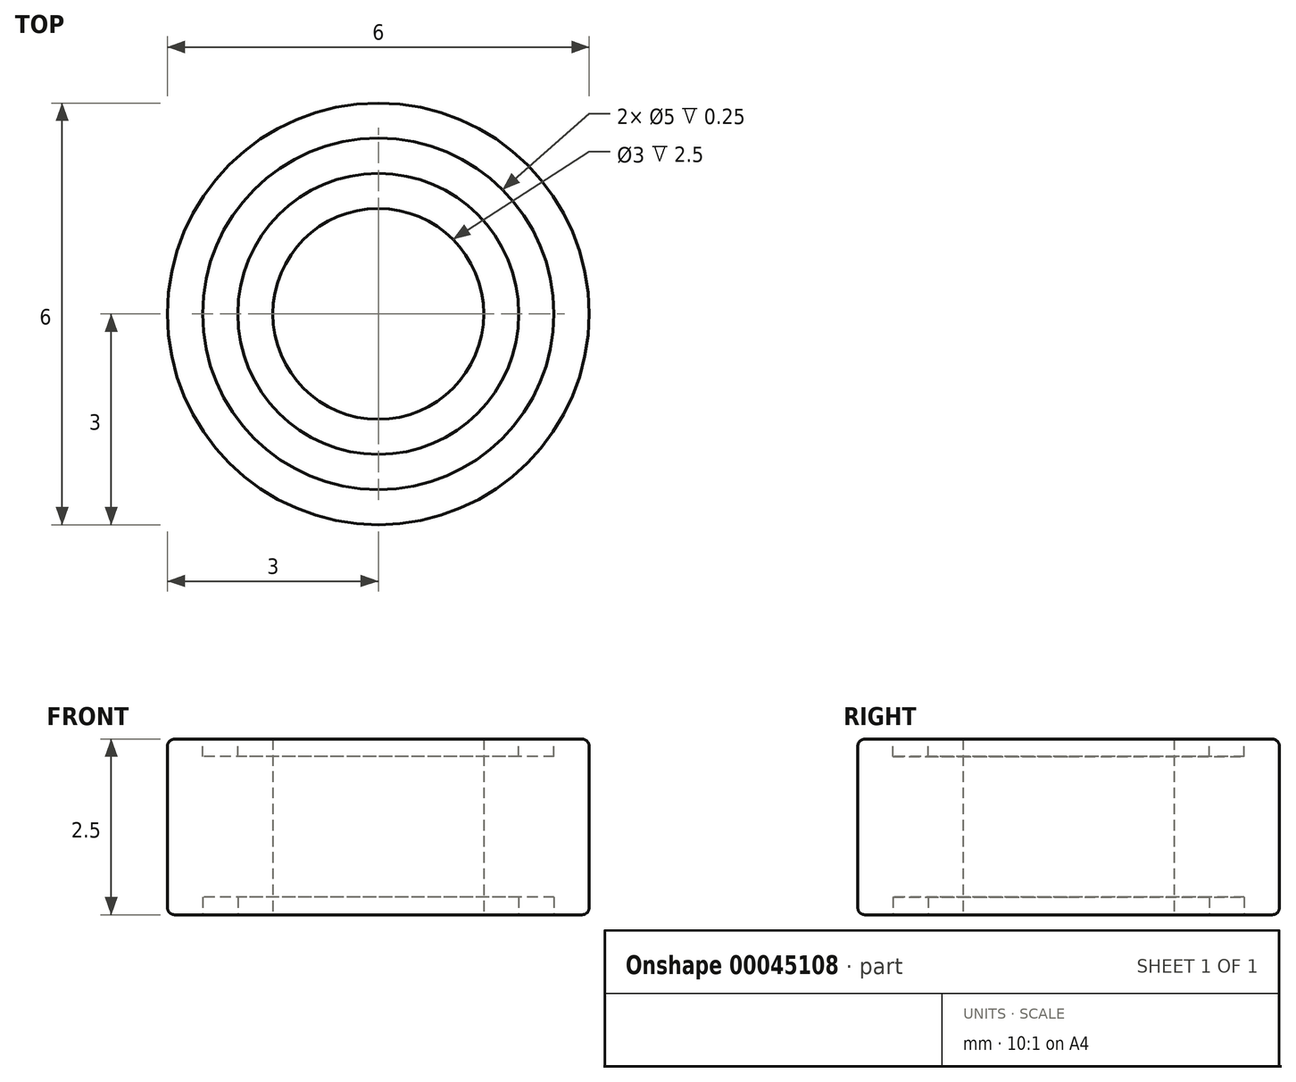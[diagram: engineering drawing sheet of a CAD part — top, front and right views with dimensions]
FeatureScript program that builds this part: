
annotation { "Feature Type Name" : "Feature", "Feature Type Description" : "" }
export const myFeature = defineFeature(function(context is Context, id is Id, definition is map)
    precondition{}
    {
        {
            var Q0;
            Q0=qCreatedBy(makeId("Top.planeOp"),FACE);
            var sketch = newSketch(context, id + "F0", { "sketchPlane" : qUnion([Q0])});
            skCircle(sketch, "E0", {"center": v(0, 0) * mm, "radius": 3 * mm});
            skCircle(sketch, "E1", {"center": v(0, 0) * mm, "radius": 1.5 * mm});
            skSolve(sketch);
        }
        {
            var Q0;
            Q0=makeQuery(id+"F0.imprint","IMPRINT",FACE,{"disambiguationData":[TD([[makeQuery(id+"F0.imprint","IMPRINT",EDGE,{"derivedFrom":sQuery(id+"F0.wireOp",EDGE,"E0")}),1.0]])]});
            extrude(context, id + "F1", {"entities" : qUnion([Q0]), "depth" : (2.5 / 2) * mm});
        }
        {
            var Q0;
            Q0=makeQuery(id+"F1.opExtrude","CAP_FACE",FACE,{"disambiguationData":[OSD([sQuery(id+"F0.wireOp",EDGE,"E0"),sQuery(id+"F0.wireOp",EDGE,"E1")])],"isStart":false});
            var sketch = newSketch(context, id + "F2", { "sketchPlane" : qUnion([Q0])});
            skCircle(sketch, "E2.0", {"center": v(0, 0) * mm, "radius": 2.5 * mm});
            skCircle(sketch, "E3.0", {"center": v(0, 0) * mm, "radius": 2 * mm});
            skSolve(sketch);
        }
        {
            var Q0;
            Q0=makeQuery(id+"F2.imprint","IMPRINT",FACE,{"disambiguationData":[TD([[makeQuery(id+"F2.imprint","IMPRINT",EDGE,{"derivedFrom":sQuery(id+"F2.wireOp",EDGE,"E2.0")}),1.0]])]});
            extrude(context, id + "F3", {"entities" : qUnion([Q0]), "operationType" : NewBodyOperationType.REMOVE, "oppositeDirection" : true, "depth" : 0.25 * mm});
        }
        {
            var Q0;
            Q0=makeQuery(id+"F1.opExtrude","SWEPT_BODY",BODY,{"disambiguationData":[OSD([sQuery(id+"F0.wireOp",EDGE,"E0"),sQuery(id+"F0.wireOp",EDGE,"E1")])]});
            var Q1;
            Q1=makeQuery(id+"F1.opExtrude","CAP_FACE",FACE,{"disambiguationData":[OSD([sQuery(id+"F0.wireOp",EDGE,"E0"),sQuery(id+"F0.wireOp",EDGE,"E1")])],"isStart":true});
            mirror(context, id + "F4", {"operationType" : NewBodyOperationType.ADD, "entities" : qUnion([Q0]), "mirrorPlane" : qUnion([Q1])});
        }
        {
            var Q0;
            {var subQ0=makeQuery(id+"F1.opExtrude","SWEPT_FACE",FACE,{"disambiguationData":[OSD([sQuery(id+"F0.wireOp",EDGE,"E0")])]});Q0=makeQuery(id+"F4.boolean.opBoolean","MERGE",FACE,{"derivedFrom":[subQ0,makeQuery(id+"F4.opPattern","COPY",FACE,{"derivedFrom":subQ0,"instanceName":"1"})]});}
            fillet(context, id + "F5", {"entities" : qUnion([Q0]), "radius" : 0.1 * mm, "tangentPropagation" : true, "allowEdgeOverflow" : false});
        }
    });
